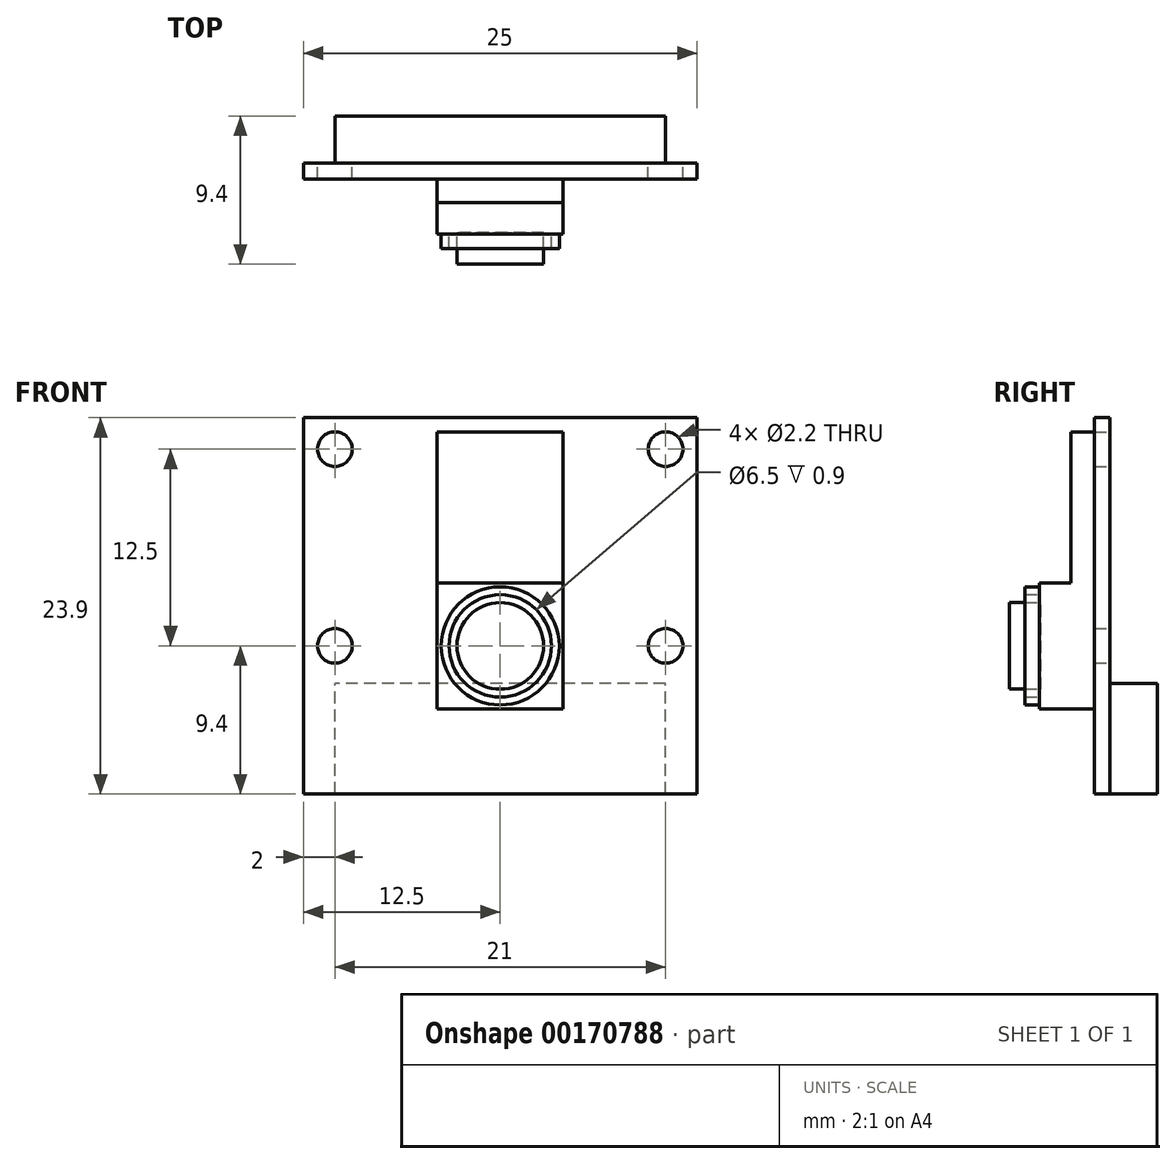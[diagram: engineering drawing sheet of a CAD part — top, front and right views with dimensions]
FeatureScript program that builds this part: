
annotation { "Feature Type Name" : "Feature", "Feature Type Description" : "" }
export const myFeature = defineFeature(function(context is Context, id is Id, definition is map)
    precondition{}
    {
        {
            var Q0;
            Q0=qCreatedBy(makeId("Front.planeOp"),FACE);
            var sketch = newSketch(context, id + "F0", { "sketchPlane" : qUnion([Q0])});
            skLineSegment(sketch, "E0.bottom", {"start": v(-12.5, 14.5) * mm, "end": v(12.5, 14.5) * mm});
            skLineSegment(sketch, "E0.top", {"start": v(-12.5, -9.4) * mm, "end": v(12.5, -9.4) * mm});
            skLineSegment(sketch, "E0.left", {"start": v(-12.5, 14.5) * mm, "end": v(-12.5, -9.4) * mm});
            skLineSegment(sketch, "E0.right", {"start": v(12.5, 14.5) * mm, "end": v(12.5, -9.4) * mm});
            skLineSegment(sketch, "E1", {"start": v(0, 14.5) * mm, "end": v(0, -9.4) * mm, "construction": true});
            skLineSegment(sketch, "E2", {"start": v(-12.5, 2.55) * mm, "end": v(12.5, 2.55) * mm, "construction": true});
            skCircle(sketch, "E3", {"center": v(-10.5, 12.5) * mm, "radius": 1.1 * mm});
            skCircle(sketch, "E4", {"center": v(-10.5, 0) * mm, "radius": 1.1 * mm});
            skCircle(sketch, "E5.MirrorC", {"center": v(10.5, 0) * mm, "radius": 1.1 * mm});
            skCircle(sketch, "E6.MirrorC", {"center": v(10.5, 12.5) * mm, "radius": 1.1 * mm});
            skSolve(sketch);
        }
        {
            var Q0;
            Q0 = qSketchRegion(id + "F0", true);
            extrude(context, id + "F1", {"entities" : qUnion([Q0]), "depth" : 1 * mm});
        }
        {
            var Q0;
            Q0=makeQuery(id+"F1.opExtrude","CAP_FACE",FACE,{"disambiguationData":[OSD([sQuery(id+"F0.wireOp",EDGE,"E0.bottom"),sQuery(id+"F0.wireOp",EDGE,"E0.top"),sQuery(id+"F0.wireOp",EDGE,"E0.left"),sQuery(id+"F0.wireOp",EDGE,"E0.right"),sQuery(id+"F0.wireOp",EDGE,"E3"),sQuery(id+"F0.wireOp",EDGE,"E4"),sQuery(id+"F0.wireOp",EDGE,"E5.MirrorC"),sQuery(id+"F0.wireOp",EDGE,"E6.MirrorC")])],"isStart":false});
            var sketch = newSketch(context, id + "F2", { "sketchPlane" : qUnion([Q0])});
            skLineSegment(sketch, "E7.bottom", {"start": v(-4, 4) * mm, "end": v(4, 4) * mm});
            skLineSegment(sketch, "E7.top", {"start": v(-4, -4) * mm, "end": v(4, -4) * mm});
            skLineSegment(sketch, "E7.left", {"start": v(-4, 4) * mm, "end": v(-4, -4) * mm});
            skLineSegment(sketch, "E7.right", {"start": v(4, 4) * mm, "end": v(4, -4) * mm});
            skLineSegment(sketch, "E8", {"start": v(0, 4) * mm, "end": v(0, -4) * mm, "construction": true});
            skLineSegment(sketch, "E9", {"start": v(-4, 0) * mm, "end": v(4, 0) * mm, "construction": true});
            skSolve(sketch);
        }
        {
            var Q0;
            Q0 = qSketchRegion(id + "F2", true);
            extrude(context, id + "F3", {"entities" : qUnion([Q0]), "operationType" : NewBodyOperationType.ADD, "depth" : 3.5 * mm});
        }
        {
            var Q0;
            Q0=makeQuery(id+"F3.opExtrude","CAP_FACE",FACE,{"disambiguationData":[OSD([sQuery(id+"F2.wireOp",EDGE,"E7.bottom"),sQuery(id+"F2.wireOp",EDGE,"E7.top"),sQuery(id+"F2.wireOp",EDGE,"E7.left"),sQuery(id+"F2.wireOp",EDGE,"E7.right")])],"isStart":false});
            var sketch = newSketch(context, id + "F4", { "sketchPlane" : qUnion([Q0])});
            skCircle(sketch, "E10", {"center": v(0, 0) * mm, "radius": 3.75 * mm});
            skCircle(sketch, "E11", {"center": v(0, 0) * mm, "radius": 3.25 * mm});
            skSolve(sketch);
        }
        {
            var Q0;
            Q0 = qSketchRegion(id + "F4", true);
            extrude(context, id + "F5", {"entities" : qUnion([Q0]), "operationType" : NewBodyOperationType.ADD, "depth" : 0.9 * mm});
        }
        {
            var Q0;
            Q0=makeQuery(id+"F5.opExtrude","CAP_FACE",FACE,{"disambiguationData":[OSD([sQuery(id+"F4.wireOp",EDGE,"E10"),sQuery(id+"F4.wireOp",EDGE,"E11")])],"isStart":false});
            var sketch = newSketch(context, id + "F6", { "sketchPlane" : qUnion([Q0])});
            skCircle(sketch, "E12", {"center": v(0, 0) * mm, "radius": 2.75 * mm});
            skSolve(sketch);
        }
        {
            var Q0;
            Q0 = qSketchRegion(id + "F6", true);
            extrude(context, id + "F7", {"entities" : qUnion([Q0]), "depth" : 1 * mm, "hasSecondDirection" : true, "secondDirectionOppositeDirection" : true, "secondDirectionDepth" : 1 * mm});
        }
        {
            var Q0;
            Q0=makeQuery(id+"F1.opExtrude","CAP_FACE",FACE,{"disambiguationData":[OSD([sQuery(id+"F0.wireOp",EDGE,"E0.bottom"),sQuery(id+"F0.wireOp",EDGE,"E0.top"),sQuery(id+"F0.wireOp",EDGE,"E0.left"),sQuery(id+"F0.wireOp",EDGE,"E0.right"),sQuery(id+"F0.wireOp",EDGE,"E3"),sQuery(id+"F0.wireOp",EDGE,"E4"),sQuery(id+"F0.wireOp",EDGE,"E5.MirrorC"),sQuery(id+"F0.wireOp",EDGE,"E6.MirrorC")])],"isStart":false});
            var sketch = newSketch(context, id + "F8", { "sketchPlane" : qUnion([Q0])});
            skLineSegment(sketch, "E13.bottom", {"start": v(-4, 13.59) * mm, "end": v(4, 13.59) * mm});
            skLineSegment(sketch, "E13.top", {"start": v(-4, 3.99) * mm, "end": v(4, 3.99) * mm});
            skLineSegment(sketch, "E13.left", {"start": v(-4, 13.59) * mm, "end": v(-4, 3.99) * mm});
            skLineSegment(sketch, "E13.right", {"start": v(4, 13.59) * mm, "end": v(4, 3.99) * mm});
            skSolve(sketch);
        }
        {
            var Q0;
            Q0 = qSketchRegion(id + "F8", true);
            extrude(context, id + "F9", {"entities" : qUnion([Q0]), "operationType" : NewBodyOperationType.ADD, "depth" : 1.5 * mm});
        }
        {
            var Q0;
            Q0=makeQuery(id+"F1.opExtrude","CAP_FACE",FACE,{"disambiguationData":[OSD([sQuery(id+"F0.wireOp",EDGE,"E0.bottom"),sQuery(id+"F0.wireOp",EDGE,"E0.top"),sQuery(id+"F0.wireOp",EDGE,"E0.left"),sQuery(id+"F0.wireOp",EDGE,"E0.right"),sQuery(id+"F0.wireOp",EDGE,"E3"),sQuery(id+"F0.wireOp",EDGE,"E4"),sQuery(id+"F0.wireOp",EDGE,"E5.MirrorC"),sQuery(id+"F0.wireOp",EDGE,"E6.MirrorC")])],"isStart":true});
            var sketch = newSketch(context, id + "F10", { "sketchPlane" : qUnion([Q0])});
            skLineSegment(sketch, "E14.bottom", {"start": v(-10.5, -9.4) * mm, "end": v(10.5, -9.4) * mm});
            skLineSegment(sketch, "E14.top", {"start": v(-10.5, -2.4) * mm, "end": v(10.5, -2.4) * mm});
            skLineSegment(sketch, "E14.left", {"start": v(-10.5, -9.4) * mm, "end": v(-10.5, -2.4) * mm});
            skLineSegment(sketch, "E14.right", {"start": v(10.5, -9.4) * mm, "end": v(10.5, -2.4) * mm});
            skSolve(sketch);
        }
        {
            var Q0;
            Q0 = qSketchRegion(id + "F10", true);
            extrude(context, id + "F11", {"entities" : qUnion([Q0]), "operationType" : NewBodyOperationType.ADD, "depth" : 3 * mm});
        }
    });
